# Revit family: Food-Service-Equipment_Oscartek_Gem_Ice-Cream-R4-and-S3
name_source: partatom
category: Specialty Equipment
units: mm (PartAtom-declared; Revit-internal decimal feet)

## family parameters
Always vertical = Yes
Classification Number = 23.40.40.11
Cut with Voids When Loaded = No
Enable Cutting in Views = No
Maintain Annotation Orientation = No
Part Type = Normal
Room Calculation Point = No
Round Connector Dimension = Use Diameter
Shared = No
Work Plane-Based = No

## types (3) — shared parameters
Apparent Power = 0 VA
Building Codes = https://www.arcat.com
CSI Master Format = Foodservice Shelving
CSI MasterFormat = 11 41 33
Conn Conduit = Yes
Construction Details = http://www.oscartek.com
Cycle = 60 Hz
Default Elevation = 0"
Depth = 34 1/4"
Description = GEM STATIC GELATO SHOWCASES
FL Amps = 0 A
Green Building-LEED = https://www.arcat.com
Height = 53 9/16"
Indirect Waste Connection Height = 0"
Indirect Waste Flow = 0 GPM
Indirect Waste Size = 1"
Installation-Fabrication = http://www.oscartek.com
Manufacturer = OSCARTEK
Manufacturer Fax = 650-342-7400
Manufacturer Website = http://www.oscartek.com
Max Overcurrent Protection = 0 A
Min Ckt Ampacity = 0 A
Phase = 1
Product Data = http://www.oscartek.com
Revision = R1_2018-10
Sales Information = http://www.oscartek.com
Specification = https://www.arcat.com
Test Data = http://www.oscartek.com
Type Comments = As Specified
URL = www.oscartek.com
URL Cutsheet = www.oscartek.com
Volts = 120 V
Watts = 0 W
zero-valued in all types: Weight in Pounds

## per-type parameters (varying)
| type | Container | Electrical Panel Dimension | Length | Model |
| GEM STATIC 1500-78_120/60/1 | 7 | 28 15/16" | 78 3/4" | GEM STATIC 1500-78 |
| GEM STATIC 1500-59_120/60/1 | 5 | 22 3/8" | 59 1/16" | GEM STATIC 1500-59 |
| GEM STATIC 1000-39_120/60/1 | 3 | 17 3/8" | 39 3/8" | GEM STATIC 1000-39 |

## geometry (parser evidence)
native form markers: Blend x6, Sweep x4
no freeform markers — native parametric forms only
